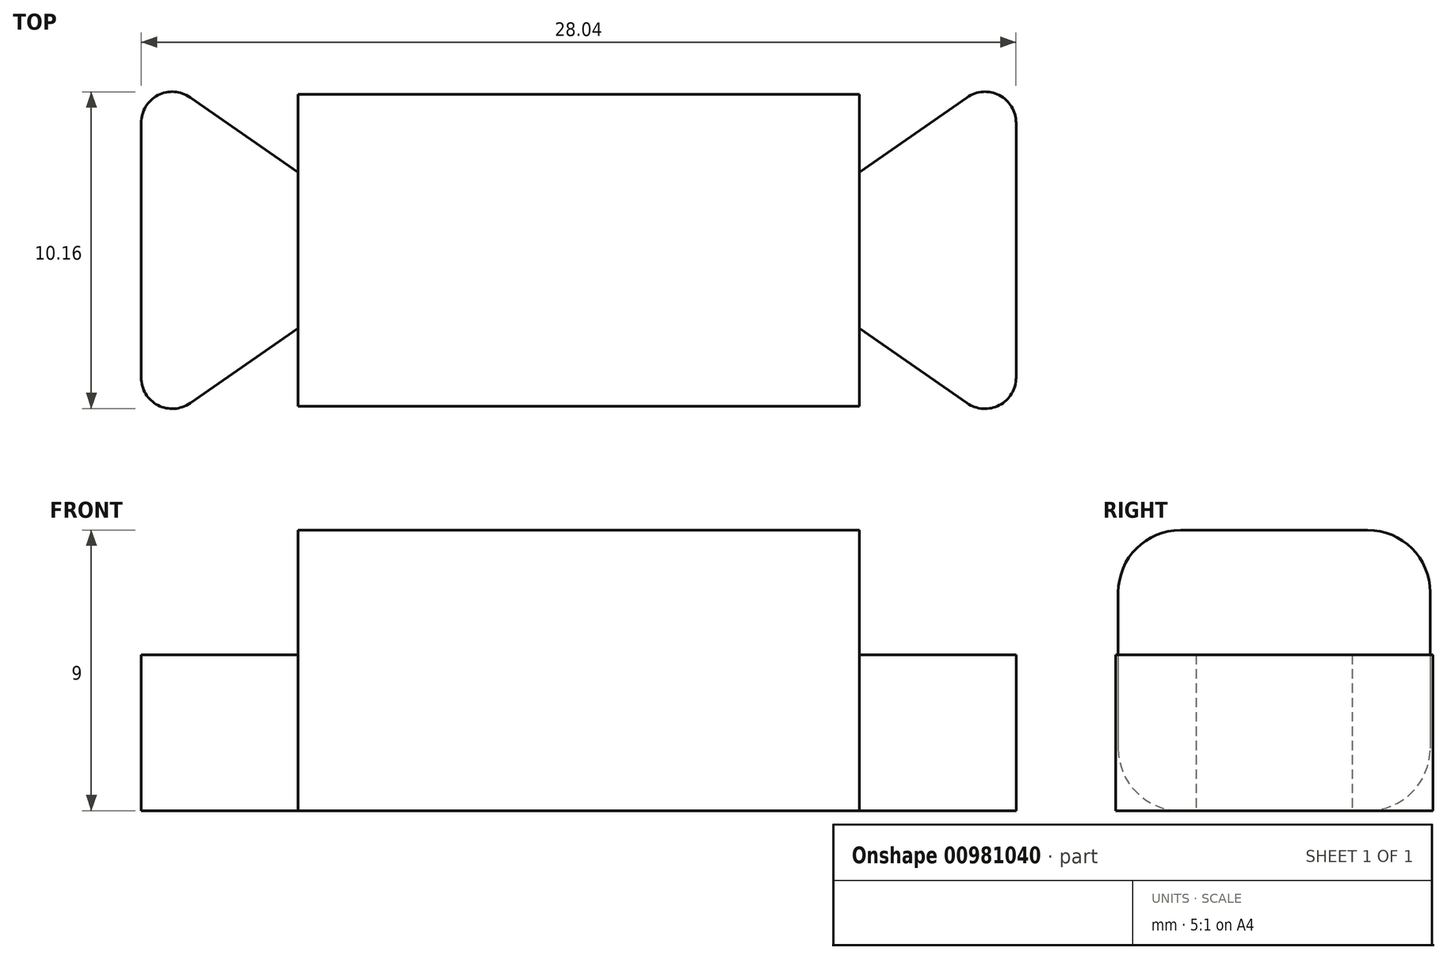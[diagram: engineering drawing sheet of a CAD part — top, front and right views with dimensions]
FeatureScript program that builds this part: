
annotation { "Feature Type Name" : "Feature", "Feature Type Description" : "" }
export const myFeature = defineFeature(function(context is Context, id is Id, definition is map)
    precondition{}
    {
        {
            var Q0;
            Q0=qCreatedBy(makeId("Top.planeOp"),FACE);
            var sketch = newSketch(context, id + "F0", { "sketchPlane" : qUnion([Q0])});
            skLineSegment(sketch, "E0.bottom", {"start": v(0, 5) * mm, "end": v(9, 5) * mm});
            skLineSegment(sketch, "E0.top", {"start": v(0, -5) * mm, "end": v(9, -5) * mm});
            skLineSegment(sketch, "E0.right", {"start": v(9, 5) * mm, "end": v(9, -5) * mm});
            skPoint(sketch, "E0.middle", {"position": v(4.5, 0) * mm});
            skLineSegment(sketch, "E1", {"start": v(14.02, 6) * mm, "end": v(14.02, -6) * mm});
            skLineSegment(sketch, "E2", {"start": v(9, 5) * mm, "end": v(9, 2.5) * mm});
            skLineSegment(sketch, "E3", {"start": v(9, -5) * mm, "end": v(9, -2.5) * mm});
            skLineSegment(sketch, "E4", {"start": v(14.02, 6) * mm, "end": v(9, 2.5) * mm});
            skLineSegment(sketch, "E5", {"start": v(14.02, -6) * mm, "end": v(9, -2.5) * mm});
            skLineSegment(sketch, "E6.MirrorCS", {"start": v(0, 5) * mm, "end": v(-9, 5) * mm});
            skLineSegment(sketch, "E7.MirrorCS", {"start": v(-9, 5) * mm, "end": v(-9, -5) * mm});
            skLineSegment(sketch, "E8.MirrorCS", {"start": v(-14.02, 6) * mm, "end": v(-14.02, -6) * mm});
            skLineSegment(sketch, "E9.MirrorCS", {"start": v(-14.02, -6) * mm, "end": v(-9, -2.5) * mm});
            skLineSegment(sketch, "E10.MirrorCS", {"start": v(0, -5) * mm, "end": v(-9, -5) * mm});
            skLineSegment(sketch, "E11.MirrorCS", {"start": v(-14.02, 6) * mm, "end": v(-9, 2.5) * mm});
            skPoint(sketch, "E12.end.orphan", {"position": v(14.02, 0) * mm});
            skPoint(sketch, "E12.start.orphan", {"position": v(9, 0) * mm});
            skLineSegment(sketch, "E13", {"start": v(9, 0) * mm, "end": v(14.02, 0) * mm});
            skSolve(sketch);
        }
        {
            var Q0;
            Q0=makeQuery(id+"F0.imprint","IMPRINT",FACE,{"disambiguationData":[TD([[makeQuery(id+"F0.imprint","IMPRINT",EDGE,{"derivedFrom":sQuery(id+"F0.wireOp",EDGE,"E0.bottom")}),-1.0]])]});
            extrude(context, id + "F1", {"entities" : qUnion([Q0]), "depth" : 9 * mm, "offsetDistance" : 25 * mm});
        }
        {
            var Q0;
            Q0=makeQuery(id+"F1.opExtrude","CAP_EDGE",EDGE,{"disambiguationData":[OSD([sQuery(id+"F0.wireOp",EDGE,"E0.top"),sQuery(id+"F0.wireOp",EDGE,"E10.MirrorCS")])],"isStart":false});
            var Q1;
            Q1=makeQuery(id+"F1.opExtrude","CAP_EDGE",EDGE,{"disambiguationData":[OSD([sQuery(id+"F0.wireOp",EDGE,"E0.bottom"),sQuery(id+"F0.wireOp",EDGE,"E6.MirrorCS")])],"isStart":false});
            var Q2;
            Q2=makeQuery(id+"F3.opExtrude","CAP_EDGE",EDGE,{"disambiguationData":[OSD([sQuery(id+"F0.wireOp",EDGE,"E0.top"),sQuery(id+"F0.wireOp",EDGE,"E10.MirrorCS")])],"isStart":true});
            var Q3;
            Q3=makeQuery(id+"F3.opExtrude","CAP_EDGE",EDGE,{"disambiguationData":[OSD([sQuery(id+"F0.wireOp",EDGE,"E0.bottom"),sQuery(id+"F0.wireOp",EDGE,"E6.MirrorCS")])],"isStart":true});
            var Q4;
            Q4=makeQuery(id+"F1.opExtrude","CAP_EDGE",EDGE,{"disambiguationData":[OSD([sQuery(id+"F0.wireOp",EDGE,"E0.bottom"),sQuery(id+"F0.wireOp",EDGE,"E6.MirrorCS")])],"isStart":true});
            var Q5;
            Q5=makeQuery(id+"F1.opExtrude","CAP_EDGE",EDGE,{"disambiguationData":[OSD([sQuery(id+"F0.wireOp",EDGE,"E0.top"),sQuery(id+"F0.wireOp",EDGE,"E10.MirrorCS")])],"isStart":true});
            fillet(context, id + "F2", {"entities" : qUnion([Q0, Q1, Q2, Q3, Q4, Q5]), "radius" : 2 * mm, "tangentPropagation" : true, "allowEdgeOverflow" : false});
        }
        {
            var Q0;
            Q0=makeQuery(id+"F0.imprint","IMPRINT",FACE,{"disambiguationData":[TD([[makeQuery(id+"F0.imprint","IMPRINT",EDGE,{"derivedFrom":sQuery(id+"F0.wireOp",EDGE,"E0.right")}),1.0]])]});
            var Q1;
            Q1=makeQuery(id+"F0.imprint","IMPRINT",FACE,{"disambiguationData":[TD([[makeQuery(id+"F0.imprint","IMPRINT",EDGE,{"derivedFrom":sQuery(id+"F0.wireOp",EDGE,"E8.MirrorCS")}),1.0]])]});
            extrude(context, id + "F3", {"entities" : qUnion([Q0, Q1]), "operationType" : NewBodyOperationType.ADD, "depth" : 5 * mm, "offsetDistance" : 25 * mm});
        }
        {
            var Q0;
            Q0=makeQuery(id+"F3.opExtrude","SWEPT_EDGE",EDGE,{"disambiguationData":[OSD([sQuery(id+"F0.wireOp",EDGE,"E8.MirrorCS"),sQuery(id+"F0.wireOp",EDGE,"E11.MirrorCS")])]});
            var Q1;
            Q1=makeQuery(id+"F3.opExtrude","SWEPT_EDGE",EDGE,{"disambiguationData":[OSD([sQuery(id+"F0.wireOp",EDGE,"E8.MirrorCS"),sQuery(id+"F0.wireOp",EDGE,"E9.MirrorCS")])]});
            var Q2;
            Q2=makeQuery(id+"F3.opExtrude","SWEPT_EDGE",EDGE,{"disambiguationData":[OSD([sQuery(id+"F0.wireOp",EDGE,"E1"),sQuery(id+"F0.wireOp",EDGE,"E5")])]});
            var Q3;
            Q3=makeQuery(id+"F3.opExtrude","SWEPT_EDGE",EDGE,{"disambiguationData":[OSD([sQuery(id+"F0.wireOp",EDGE,"E1"),sQuery(id+"F0.wireOp",EDGE,"E4")])]});
            fillet(context, id + "F4", {"entities" : qUnion([Q0, Q1, Q2, Q3]), "radius" : 1 * mm, "tangentPropagation" : true, "allowEdgeOverflow" : false});
        }
    });
